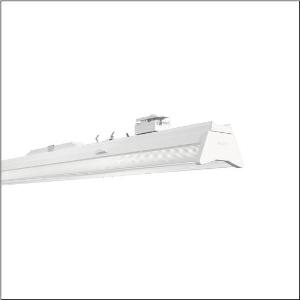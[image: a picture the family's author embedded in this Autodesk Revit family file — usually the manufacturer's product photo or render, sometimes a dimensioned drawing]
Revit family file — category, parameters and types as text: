
# Revit family: licross_r__11_performance_mo_51tm16cn49xg_d1b9
name_source: partatom
category: Lighting Fixtures
units: mm (PartAtom-declared; Revit-internal decimal feet)

## family parameters
Cut with Voids When Loaded = No
Host = Face
Light Source = No
Part Type = Normal
Room Calculation Point = No
Round Connector Dimension = Use Diameter
Shared = No

## types (1)
- --- (1 x LED, 9190 lm, 49.4 W, 4000K)
    Apparent Load = 49 VA
    CIE Flux Codes = 66 88 96 79 100
    Color Rendering = 80
    Color Temperature = 4000K
    Default Elevation = 1800 mm
    Description = Licross® 11 Performance MO, luminaire insert, of sheet steel, galvanised, coil coated, white, length: 1.500mm, width: 120mm, height: 123mm, LED rated luminous flux: 9.190lm, light colour: 840, control gear: ON/OFF Multilumen, CLOi, with plug, 3-pole, with phase selection, mains connection: 220..240V, AC, 50/60Hz, start of lifetime: 49W, end of service life: 55W, halogen-free wiring, primary light control with lens, of plastic, primary optical cover: cover, of PMMA, light emission: direct/indirect distribution, primary light characteristic: symmetric, protection rating (complete): IP40, insulation class (complete): insulation class I (protective earthing), certification: CE, ENEC, VDE, UKCA, protection symbol: D if used in an environment without relevant dust loads with corresponding accessories, impact resistance: IK06, permissible ambient temperature for indoor applications: -35..+40°C, corresponds to IFS (International Featured Standards) requirements for safety and quality in the food industry, reducing of maximum allowable ambient temperature of 5°C with ceiling mounting, LABS conformity tested according to VDMA 24364:2018-05, packaging unit: 1 piece
    Height = 114 mm
    Lamp = 1 x LED
    Lamp Light Flux = 9190 lm
    Lamp Power = 49.4 W
    Lamp count = 1
    Length = 1500 mm
    Luminous efficacy = 186 lm/W
    Manufacturer = Siteco
    ModVariant = No
    Model = 51TM16CN49XG
    Mounting Place = Ceiling
    Mounting Type = Pendant
    Number of Poles = 1
    OnlyDefault = Yes
    Power Factor = 1
    Product Name = Licross® 11 Performance MO
    Product group = luminaire insert
    ProductGroupID = 901
    Protection Class = Protection class I
    Protection Degree = IP 40
    RLX_Detail_Level = 1
    RLX_Emergency_Light_Flux = 0 lm
    RLX_Emergency_Type = 0
    RLX_Emergency_Type_DB = No
    RlxData = <blob elided: 31797 chars, md5=951a11a4>
    Socket = socket
    Standby Power = 0 W
    System Light Flux = 9190 lm
    System Power = 49 W
    Type Comments = factory setting: luminous flux: 100 % | (A | C | E) | 113 mA
    Type Image = l_1256138.jpg
    URL = http://relux.com
    VarID = @adj_038287
    Voltage = 0 V
    Weight = 0.00 kg
    Width = 120 mm

## geometry (parser evidence)
native form markers: Blend x4, Sweep x11
no freeform markers — native parametric forms only
